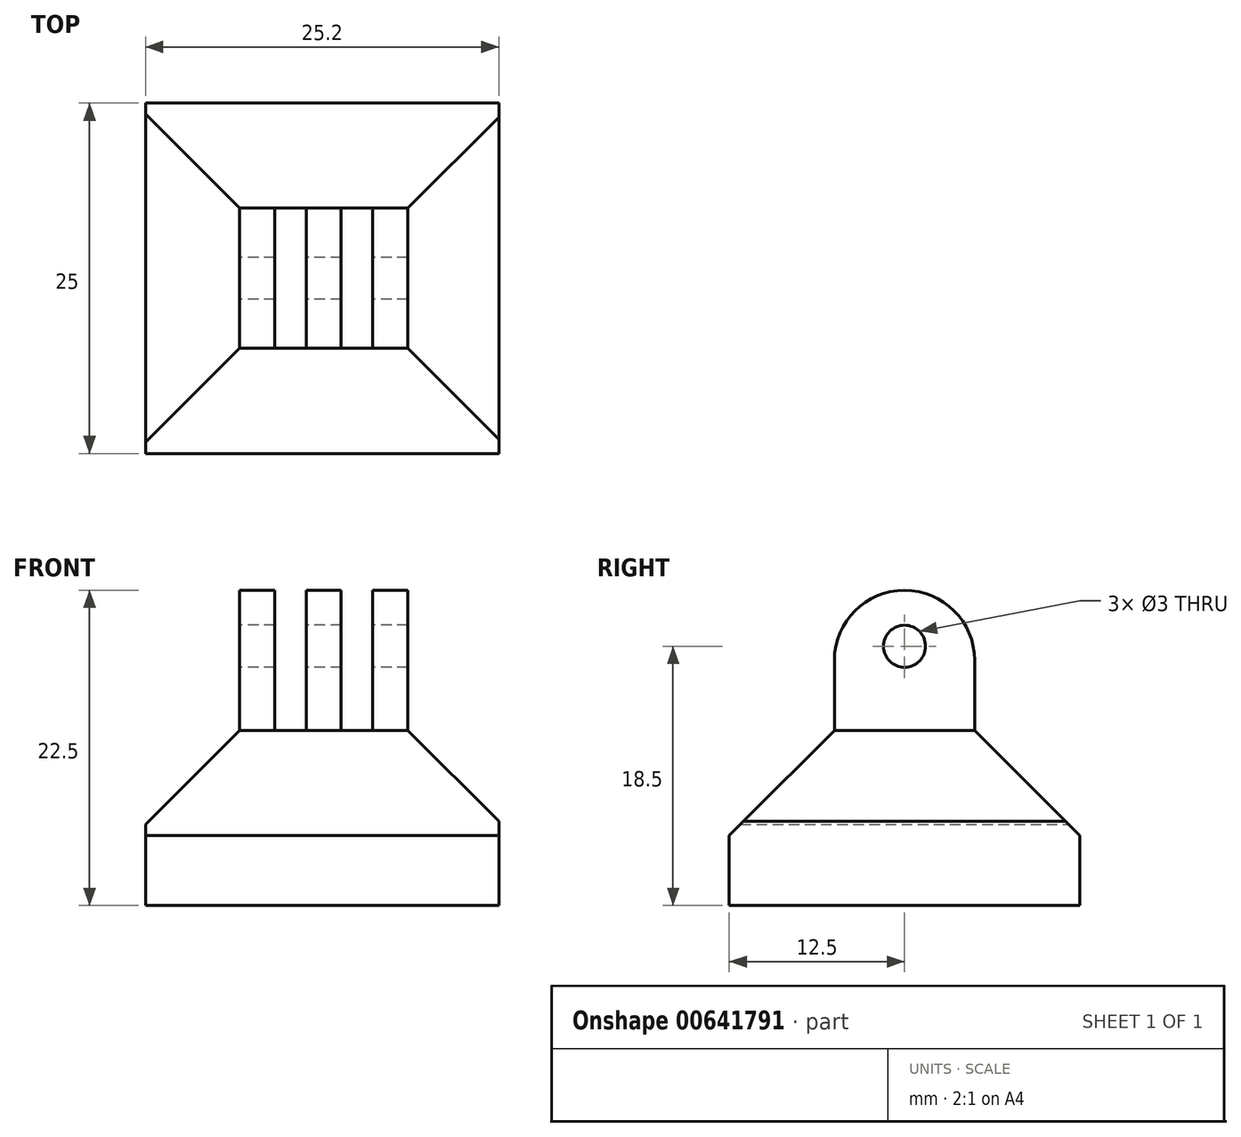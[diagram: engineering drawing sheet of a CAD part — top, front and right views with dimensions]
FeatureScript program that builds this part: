
annotation { "Feature Type Name" : "Feature", "Feature Type Description" : "" }
export const myFeature = defineFeature(function(context is Context, id is Id, definition is map)
    precondition{}
    {
        {
            var Q0;
            Q0=qCreatedBy(makeId("Front.planeOp"),FACE);
            var sketch = newSketch(context, id + "F0", { "sketchPlane" : qUnion([Q0])});
            skLineSegment(sketch, "E0.bottom", {"start": v(12.5, 2.5) * mm, "end": v(-12.5, 2.5) * mm});
            skLineSegment(sketch, "E0.top", {"start": v(12.5, -2.5) * mm, "end": v(-12.5, -2.5) * mm});
            skLineSegment(sketch, "E0.left", {"start": v(12.5, 2.5) * mm, "end": v(12.5, -2.5) * mm});
            skLineSegment(sketch, "E0.right", {"start": v(-12.5, 2.5) * mm, "end": v(-12.5, -2.5) * mm});
            skPoint(sketch, "E0.middle", {"position": v(0, 0) * mm});
            skLineSegment(sketch, "E1", {"start": v(-6, 10) * mm, "end": v(-6, 20) * mm});
            skLineSegment(sketch, "E2", {"start": v(-6, 20) * mm, "end": v(-3.5, 20) * mm});
            skLineSegment(sketch, "E3", {"start": v(-3.5, 20) * mm, "end": v(-3.5, 10) * mm});
            skLineSegment(sketch, "E4", {"start": v(-3.5, 10) * mm, "end": v(-1.25, 10) * mm});
            skLineSegment(sketch, "E5", {"start": v(-1.25, 10) * mm, "end": v(-1.25, 20) * mm});
            skLineSegment(sketch, "E6", {"start": v(-1.25, 20) * mm, "end": v(0, 20) * mm});
            skLineSegment(sketch, "E7.MirrorCS", {"start": v(1.25, 20) * mm, "end": v(0, 20) * mm});
            skLineSegment(sketch, "E8.MirrorCS", {"start": v(1.25, 10) * mm, "end": v(1.25, 20) * mm});
            skLineSegment(sketch, "E9.MirrorCS", {"start": v(3.5, 10) * mm, "end": v(1.25, 10) * mm});
            skLineSegment(sketch, "E10.MirrorCS", {"start": v(3.5, 20) * mm, "end": v(3.5, 10) * mm});
            skLineSegment(sketch, "E11.MirrorCS", {"start": v(6, 10) * mm, "end": v(6, 20) * mm});
            skLineSegment(sketch, "E12.MirrorCS", {"start": v(6, 20) * mm, "end": v(3.5, 20) * mm});
            skLineSegment(sketch, "E13", {"start": v(-6, 10) * mm, "end": v(-6, 2.5) * mm});
            skLineSegment(sketch, "E14", {"start": v(6, 10) * mm, "end": v(6, 2.5) * mm});
            skSolve(sketch);
        }
        {
            var Q0;
            Q0 = qSketchRegion(id + "F0", true);
            extrude(context, id + "F1", {"entities" : qUnion([Q0]), "depth" : 10 * mm, "offsetDistance" : 25 * mm});
        }
        {
            var Q0;
            Q0=makeQuery(id+"F1.opExtrude","CAP_EDGE",EDGE,{"disambiguationData":[OSD([sQuery(id+"F0.wireOp",EDGE,"E2")])],"isStart":true});
            var Q1;
            Q1=makeQuery(id+"F1.opExtrude","CAP_EDGE",EDGE,{"disambiguationData":[OSD([sQuery(id+"F0.wireOp",EDGE,"E6"),sQuery(id+"F0.wireOp",EDGE,"E7.MirrorCS")])],"isStart":true});
            var Q2;
            Q2=makeQuery(id+"F1.opExtrude","CAP_EDGE",EDGE,{"disambiguationData":[OSD([sQuery(id+"F0.wireOp",EDGE,"E12.MirrorCS")])],"isStart":true});
            var Q3;
            Q3=makeQuery(id+"F1.opExtrude","CAP_EDGE",EDGE,{"disambiguationData":[OSD([sQuery(id+"F0.wireOp",EDGE,"E2")])],"isStart":false});
            var Q4;
            Q4=makeQuery(id+"F1.opExtrude","CAP_EDGE",EDGE,{"disambiguationData":[OSD([sQuery(id+"F0.wireOp",EDGE,"E6"),sQuery(id+"F0.wireOp",EDGE,"E7.MirrorCS")])],"isStart":false});
            var Q5;
            Q5=makeQuery(id+"F1.opExtrude","CAP_EDGE",EDGE,{"disambiguationData":[OSD([sQuery(id+"F0.wireOp",EDGE,"E12.MirrorCS")])],"isStart":false});
            fillet(context, id + "F2", {"entities" : qUnion([Q0, Q1, Q2, Q3, Q4, Q5]), "radius" : 5 * mm, "tangentPropagation" : true, "allowEdgeOverflow" : false});
        }
        {
            var Q0;
            Q0=makeQuery(id+"F1.opExtrude","SWEPT_FACE",FACE,{"disambiguationData":[OSD([sQuery(id+"F0.wireOp",EDGE,"E0.left")])]});
            var sketch = newSketch(context, id + "F3", { "sketchPlane" : qUnion([Q0])});
            skLineSegment(sketch, "E15.bottom", {"start": v(-17.5, 2.5) * mm, "end": v(7.5, 2.5) * mm});
            skLineSegment(sketch, "E15.top", {"start": v(-17.5, -2.5) * mm, "end": v(7.5, -2.5) * mm});
            skLineSegment(sketch, "E15.left", {"start": v(-17.5, 2.5) * mm, "end": v(-17.5, -2.5) * mm});
            skLineSegment(sketch, "E15.right", {"start": v(7.5, 2.5) * mm, "end": v(7.5, -2.5) * mm});
            skSolve(sketch);
        }
        {
            var Q0;
            {var subQ2=sQuery(id+"F3.wireOp",EDGE,"E15.left");Q0=makeQuery(id+"F3.imprint","IMPRINT",FACE,{"disambiguationData":[TD([[makeQuery(id+"F3.imprint","IMPRINT",EDGE,{"derivedFrom":subQ2}),1.0]])]});}
            var Q1;
            {var subQ2=sQuery(id+"F3.wireOp",EDGE,"E15.right");Q1=makeQuery(id+"F3.imprint","IMPRINT",FACE,{"disambiguationData":[TD([[makeQuery(id+"F3.imprint","IMPRINT",EDGE,{"derivedFrom":subQ2}),-1.0]])]});}
            var Q2;
            {var subQ1=sQuery(id+"F0.wireOp",EDGE,"E0.left");var subQ2=makeQuery(id+"F1.opExtrude","CAP_EDGE",EDGE,{"disambiguationData":[OSD([subQ1])],"isStart":true});Q2=makeQuery(id+"F3.imprint","IMPRINT",FACE,{"disambiguationData":[TD([[makeQuery(id+"F3.imprint","IMPRINT",EDGE,{"derivedFrom":subQ2}),-1.0]])]});}
            extrude(context, id + "F4", {"entities" : qUnion([Q0, Q1, Q2]), "operationType" : NewBodyOperationType.ADD, "oppositeDirection" : true, "depth" : 25.2 * mm, "offsetDistance" : 25 * mm});
        }
        {
            var Q0;
            Q0=makeQuery(id+"F4.boolean.opBoolean","INTERSECT",EDGE,{"derivedFrom":[makeQuery(id+"F1.opExtrude","CAP_FACE",FACE,{"disambiguationData":[OSD([sQuery(id+"F0.wireOp",EDGE,"E0.bottom"),sQuery(id+"F0.wireOp",EDGE,"E0.top"),sQuery(id+"F0.wireOp",EDGE,"E0.left"),sQuery(id+"F0.wireOp",EDGE,"E0.right"),sQuery(id+"F0.wireOp",EDGE,"E1"),sQuery(id+"F0.wireOp",EDGE,"E2"),sQuery(id+"F0.wireOp",EDGE,"E3"),sQuery(id+"F0.wireOp",EDGE,"E4"),sQuery(id+"F0.wireOp",EDGE,"E5"),sQuery(id+"F0.wireOp",EDGE,"E6"),sQuery(id+"F0.wireOp",EDGE,"E7.MirrorCS"),sQuery(id+"F0.wireOp",EDGE,"E8.MirrorCS"),sQuery(id+"F0.wireOp",EDGE,"E9.MirrorCS"),sQuery(id+"F0.wireOp",EDGE,"E10.MirrorCS"),sQuery(id+"F0.wireOp",EDGE,"E11.MirrorCS"),sQuery(id+"F0.wireOp",EDGE,"E12.MirrorCS"),sQuery(id+"F0.wireOp",EDGE,"E13"),sQuery(id+"F0.wireOp",EDGE,"E14")])],"isStart":false}),makeQuery(id+"F4.opExtrude","SWEPT_FACE",FACE,{"disambiguationData":[OSD([sQuery(id+"F3.wireOp",EDGE,"E15.bottom")])]})]});
            var Q1;
            Q1=makeQuery(id+"F1.opExtrude","SWEPT_EDGE",EDGE,{"disambiguationData":[OSD([sQuery(id+"F0.wireOp",EDGE,"E0.bottom"),sQuery(id+"F0.wireOp",EDGE,"E14")])]});
            var Q2;
            Q2=makeQuery(id+"F4.boolean.opBoolean","INTERSECT",EDGE,{"derivedFrom":[makeQuery(id+"F1.opExtrude","CAP_FACE",FACE,{"disambiguationData":[OSD([sQuery(id+"F0.wireOp",EDGE,"E0.bottom"),sQuery(id+"F0.wireOp",EDGE,"E0.top"),sQuery(id+"F0.wireOp",EDGE,"E0.left"),sQuery(id+"F0.wireOp",EDGE,"E0.right"),sQuery(id+"F0.wireOp",EDGE,"E1"),sQuery(id+"F0.wireOp",EDGE,"E2"),sQuery(id+"F0.wireOp",EDGE,"E3"),sQuery(id+"F0.wireOp",EDGE,"E4"),sQuery(id+"F0.wireOp",EDGE,"E5"),sQuery(id+"F0.wireOp",EDGE,"E6"),sQuery(id+"F0.wireOp",EDGE,"E7.MirrorCS"),sQuery(id+"F0.wireOp",EDGE,"E8.MirrorCS"),sQuery(id+"F0.wireOp",EDGE,"E9.MirrorCS"),sQuery(id+"F0.wireOp",EDGE,"E10.MirrorCS"),sQuery(id+"F0.wireOp",EDGE,"E11.MirrorCS"),sQuery(id+"F0.wireOp",EDGE,"E12.MirrorCS"),sQuery(id+"F0.wireOp",EDGE,"E13"),sQuery(id+"F0.wireOp",EDGE,"E14")])],"isStart":true}),makeQuery(id+"F4.opExtrude","SWEPT_FACE",FACE,{"disambiguationData":[OSD([sQuery(id+"F3.wireOp",EDGE,"E15.bottom")])]})]});
            var Q3;
            Q3=makeQuery(id+"F1.opExtrude","SWEPT_EDGE",EDGE,{"disambiguationData":[OSD([sQuery(id+"F0.wireOp",EDGE,"E0.bottom"),sQuery(id+"F0.wireOp",EDGE,"E13")])]});
            chamfer(context, id + "F5", {"entities" : qUnion([Q0, Q1, Q2, Q3]), "width" : 7.5 * mm, "tangentPropagation" : true});
        }
        {
            var Q0;
            Q0=makeQuery(id+"F1.opExtrude","SWEPT_FACE",FACE,{"disambiguationData":[OSD([sQuery(id+"F0.wireOp",EDGE,"E1"),sQuery(id+"F0.wireOp",EDGE,"E13")])]});
            var sketch = newSketch(context, id + "F6", { "sketchPlane" : qUnion([Q0])});
            skCircle(sketch, "E16", {"center": v(5, 16) * mm, "radius": 1.5 * mm});
            skPoint(sketch, "E16.centerSnap0", {"position": v(5, 20) * mm});
            skSolve(sketch);
        }
        {
            var Q0;
            Q0=makeQuery(id+"F6.imprint","IMPRINT",FACE,{"disambiguationData":[TD([[makeQuery(id+"F6.imprint","IMPRINT",EDGE,{"derivedFrom":sQuery(id+"F6.wireOp",EDGE,"E16")}),1.0]])]});
            extrude(context, id + "F7", {"entities" : qUnion([Q0]), "operationType" : NewBodyOperationType.REMOVE, "oppositeDirection" : true, "depth" : 25 * mm, "offsetDistance" : 25 * mm});
        }
    });
